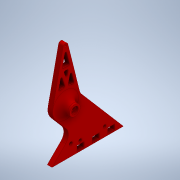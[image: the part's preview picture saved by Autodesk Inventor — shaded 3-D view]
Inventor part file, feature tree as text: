
AUTODESK INVENTOR PART (.ipt)
format: ipt  version: 2020 (Build 240168000, 168)  size: 323,584 bytes
history: native  units: mm
features: extrude x7, sketch x7, other x3, fillet x1, chamfer x1, projected_geometry x1
ambient origin geometry x8: Origin, YZ Plane, XZ Plane, XY Plane, X Axis, Y Axis, Z Axis, Center Point
bodies: Solid1 (feature_tree)
feature tree (20):
  other  "WeaponMountBasePlateV1.ipt"
  extrude  "Extrusion1"  Depth=10.0mm
  extrude  "Extrusion2"  TaperAngle=0.0deg  [1 undecoded]
  extrude  "Extrusion3"  Depth=1.0mm
  fillet  "Fillet2"  [1 undecoded]
  extrude  "Extrusion4"  Depth=1.65mm
  extrude  "Extrusion5"  Depth=8.0mm
  extrude  "Extrusion6"  Depth=10.0mm TaperAngle=0.0deg
  chamfer  "Chamfer1"  [1 undecoded]
  extrude  "Extrusion7"  Depth=2.0mm
  other  "Solid1::WeaponMountBasePlateV1.ipt"
  other  "TaggingFeature1"
  sketch  "Sketch2"  dims[d0=10.0mm d2=11.3mm]
  sketch  "Sketch3"  dims[d3=10.0mm d4=0.0mm]
  sketch  "Sketch4"  dims[d5=7.3mm d6=1.0mm d7=0.0mm]
  projected_geometry  "Projected Loop1"
  sketch  "Sketch5"  dims[d8=7.3mm d9=1.65mm]
  sketch  "Sketch6"  dims[d10=0.0mm d12=8.0mm]
  sketch  "Sketch7"  dims[d13=4.5mm d14=10.0mm d15=0.0mm]
  sketch  "Sketch8"  dims[d16=2.2mm d17=0.0mm d18=0.0mm d19=4.0mm d20=2.0mm d21=0.0mm d22=0.9mm d23=2.0mm d24=45.0deg d25=6.1mm d26=0.0mm d27=-7.853982mm]
note: 3 required parameter values undecoded (feature->parameter linkage not recoverable at this tier; creation-order binding heuristic only, values carry confidence <= 0.55)
